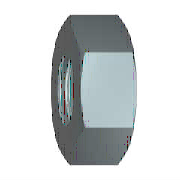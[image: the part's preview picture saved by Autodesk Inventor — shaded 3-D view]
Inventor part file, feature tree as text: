
AUTODESK INVENTOR PART (.ipt)
format: ipt  version: 2022 (Build 260153000, 153)  size: 173,056 bytes
history: native  units: mm (DEFAULTED — no unit token found)
features: sketch x3, other x2, extrude x1, hole x1, plane x1
ambient origin geometry x7: Origin, YZ Plane, XZ Plane, X Axis, Y Axis, Z Axis, Center Point
bodies: Solid1 (feature_tree)
feature tree (8):
  extrude  "Базовый элемент"  Depth=9.237604mm
  other  "Фаска1"
  hole  "Резьба"  [1 undecoded]
  other  "Work Axis1"
  plane  "Work Plane1"
  sketch  "Эскиз1"
  sketch  "Эскиз2"
  sketch  "Эскиз3"
note: 1 required parameter value undecoded (feature->parameter linkage not recoverable at this tier; creation-order binding heuristic only, values carry confidence <= 0.55)
